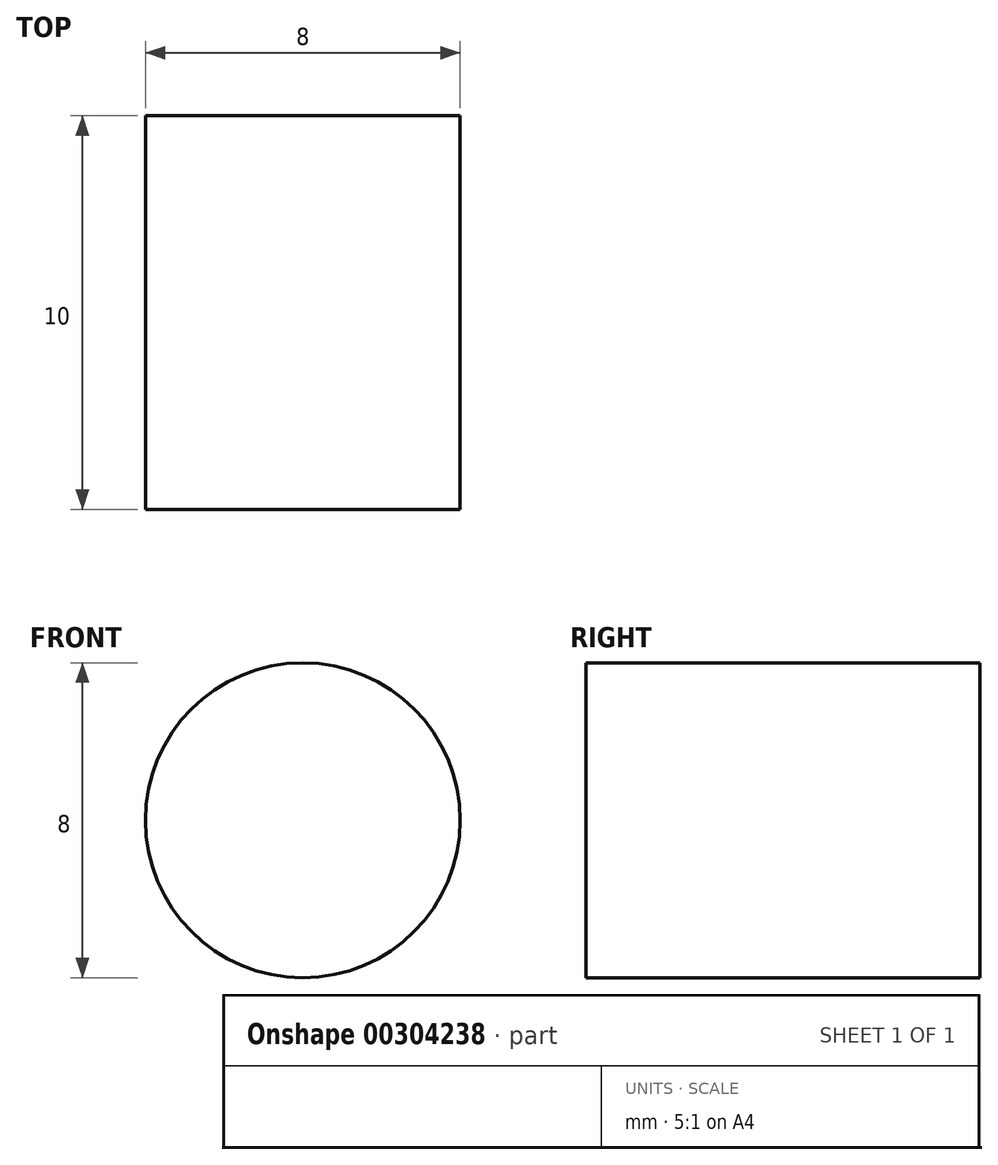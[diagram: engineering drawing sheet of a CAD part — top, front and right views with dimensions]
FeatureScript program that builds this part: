
annotation { "Feature Type Name" : "Feature", "Feature Type Description" : "" }
export const myFeature = defineFeature(function(context is Context, id is Id, definition is map)
    precondition{}
    {
        {
            var Q0;
            Q0=qCreatedBy(makeId("Front.planeOp"),FACE);
            var sketch = newSketch(context, id + "F0", { "sketchPlane" : qUnion([Q0])});
            skCircle(sketch, "E0", {"center": v(0, 0) * mm, "radius": 4 * mm});
            skSolve(sketch);
        }
        {
            var Q0;
            Q0=makeQuery(id+"F0.imprint","IMPRINT",FACE,{"disambiguationData":[TD([[makeQuery(id+"F0.imprint","IMPRINT",EDGE,{"derivedFrom":sQuery(id+"F0.wireOp",EDGE,"E0")}),1.0]])]});
            extrude(context, id + "F1", {"entities" : qUnion([Q0]), "depth" : 10 * mm});
        }
    });
